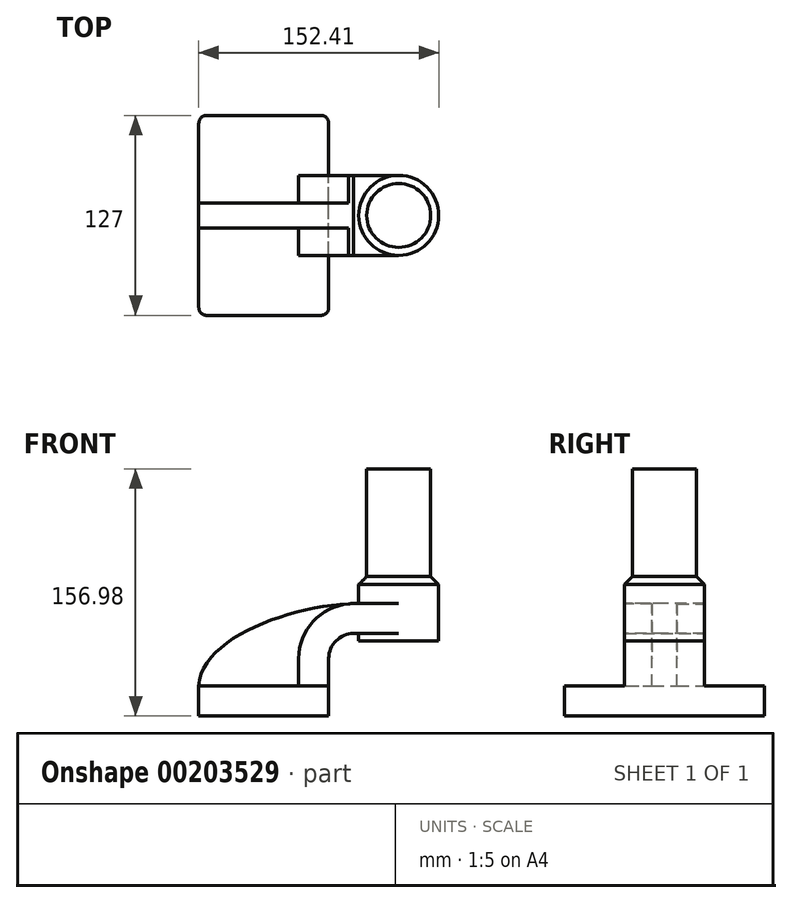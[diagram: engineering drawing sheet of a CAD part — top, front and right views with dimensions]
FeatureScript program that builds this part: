
annotation { "Feature Type Name" : "Feature", "Feature Type Description" : "" }
export const myFeature = defineFeature(function(context is Context, id is Id, definition is map)
    precondition{}
    {
        {
            var Q0;
            Q0=qCreatedBy(makeId("Front.planeOp"),FACE);
            var sketch = newSketch(context, id + "F0", { "sketchPlane" : qUnion([Q0])});
            skLineSegment(sketch, "E0.rect.bottom", {"start": v(-41.28, 9.52) * mm, "end": v(41.28, 9.52) * mm});
            skLineSegment(sketch, "E0.rect.top", {"start": v(-41.28, -9.52) * mm, "end": v(41.28, -9.52) * mm});
            skLineSegment(sketch, "E0.rect.left", {"start": v(-41.28, 9.52) * mm, "end": v(-41.28, -9.52) * mm});
            skLineSegment(sketch, "E0.rect.right", {"start": v(41.28, 9.52) * mm, "end": v(41.28, -9.52) * mm});
            skPoint(sketch, "E0.rect.middle", {"position": v(0, 0) * mm});
            skLineSegment(sketch, "E1", {"start": v(41.28, 9.52) * mm, "end": v(41.28, 27) * mm});
            skArc(sketch, "E2", {"start": v(41.28, 27) * mm, "mid": v(45.92, 38.23) * mm, "end": v(57.15, 42.88) * mm});
            skLineSegment(sketch, "E3", {"start": v(57.15, 42.88) * mm, "end": v(85.72, 42.88) * mm});
            skLineSegment(sketch, "E4.rect.bottom", {"start": v(60.32, 38.1) * mm, "end": v(111.12, 38.1) * mm});
            skLineSegment(sketch, "E4.rect.top", {"start": v(60.32, 66.68) * mm, "end": v(111.12, 66.68) * mm});
            skLineSegment(sketch, "E4.rect.left", {"start": v(60.32, 38.1) * mm, "end": v(60.32, 66.68) * mm});
            skLineSegment(sketch, "E4.rect.right", {"start": v(111.13, 38.1) * mm, "end": v(111.12, 66.68) * mm});
            skPoint(sketch, "E4.rect.middle", {"position": v(85.72, 52.39) * mm});
            skLineSegment(sketch, "E5.0", {"start": v(57.15, 61.93) * mm, "end": v(85.72, 61.93) * mm});
            skArc(sketch, "E5.1", {"start": v(22.23, 27) * mm, "mid": v(32.45, 51.7) * mm, "end": v(57.15, 61.93) * mm});
            skLineSegment(sketch, "E5.2", {"start": v(22.23, 9.52) * mm, "end": v(22.23, 27) * mm});
            skLineSegment(sketch, "E6", {"start": v(85.72, 38.1) * mm, "end": v(85.72, 66.68) * mm});
            skFitSpline(sketch, "E7", {"points": [v(-41.28, 9.53) * mm, v(57.15, 61.93) * mm], "startDerivative": vector(5.2, 92.34) * mm, "endDerivative": vector(120.92, 4.22) * mm});
            skSolve(sketch);
        }
        {
            var Q0;
            Q0=makeQuery(id+"F0.imprint","IMPRINT",FACE,{"disambiguationData":[TD([[makeQuery(id+"F0.imprint","IMPRINT",EDGE,{"derivedFrom":sQuery(id+"F0.wireOp",EDGE,"E0.rect.top")}),1.0]])]});
            extrude(context, id + "F1", {"entities" : qUnion([Q0]), "endBound" : BoundingType.SYMMETRIC, "depth" : 127 * mm});
        }
        {
            var Q0;
            {var subQ9=sQuery(id+"F0.wireOp",EDGE,"E1");Q0=makeQuery(id+"F0.imprint","IMPRINT",FACE,{"disambiguationData":[TD([[makeQuery(id+"F0.imprint","IMPRINT",EDGE,{"derivedFrom":subQ9}),1.0]])]});}
            var Q1;
            {var subQ0=sQuery(id+"F0.wireOp",EDGE,"E6");var subQ1=sQuery(id+"F0.wireOp",EDGE,"E3");var subQ2=makeQuery(id+"F0.imprint","INTERSECT",VERTEX,{"derivedFrom":[subQ1,subQ0]});Q1=makeQuery(id+"F0.imprint","IMPRINT",FACE,{"disambiguationData":[TD([[makeQuery(id+"F0.imprint","IMPRINT",EDGE,{"disambiguationData":[TD([[subQ2,1.0]])],"derivedFrom":subQ1}),1.0]])]});}
            extrude(context, id + "F2", {"entities" : qUnion([Q0, Q1]), "operationType" : NewBodyOperationType.ADD, "endBound" : BoundingType.SYMMETRIC, "depth" : 50.8 * mm});
        }
        {
            var Q0;
            {var subQ3=sQuery(id+"F0.wireOp",EDGE,"E5.2");Q0=makeQuery(id+"F0.imprint","IMPRINT",FACE,{"disambiguationData":[TD([[makeQuery(id+"F0.imprint","IMPRINT",EDGE,{"derivedFrom":subQ3}),1.0]])]});}
            extrude(context, id + "F3", {"entities" : qUnion([Q0]), "operationType" : NewBodyOperationType.ADD, "endBound" : BoundingType.SYMMETRIC, "depth" : 15.88 * mm});
        }
        {
            var Q0;
            {var subQ5=sQuery(id+"F0.wireOp",EDGE,"E4.rect.right");Q0=makeQuery(id+"F0.imprint","IMPRINT",FACE,{"disambiguationData":[TD([[makeQuery(id+"F0.imprint","IMPRINT",EDGE,{"derivedFrom":subQ5}),1.0]])]});}
            var Q1;
            Q1=sQuery(id+"F0.wireOp",EDGE,"E6");
            revolve(context, id + "F4", {"operationType" : NewBodyOperationType.ADD, "entities" : qUnion([Q0]), "axis" : qUnion([Q1]), "revolveType" : RevolveType.FULL});
        }
        {
            var Q0;
            Q0=makeQuery(id+"F1.opExtrude","CAP_EDGE",EDGE,{"disambiguationData":[OSD([sQuery(id+"F0.wireOp",EDGE,"E0.rect.right")])],"isStart":false});
            var Q1;
            Q1=makeQuery(id+"F1.opExtrude","CAP_EDGE",EDGE,{"disambiguationData":[OSD([sQuery(id+"F0.wireOp",EDGE,"E0.rect.left")])],"isStart":false});
            var Q2;
            Q2=makeQuery(id+"F1.opExtrude","CAP_EDGE",EDGE,{"disambiguationData":[OSD([sQuery(id+"F0.wireOp",EDGE,"E0.rect.right")])],"isStart":true});
            var Q3;
            Q3=makeQuery(id+"F1.opExtrude","CAP_EDGE",EDGE,{"disambiguationData":[OSD([sQuery(id+"F0.wireOp",EDGE,"E0.rect.left")])],"isStart":true});
            fillet(context, id + "F5", {"entities" : qUnion([Q0, Q1, Q2, Q3]), "radius" : 5.08 * mm, "tangentPropagation" : true, "allowEdgeOverflow" : false});
        }
        {
            var Q0;
            Q0=makeQuery(id+"F4.opRevolve","SWEPT_FACE",FACE,{"disambiguationData":[OSD([sQuery(id+"F0.wireOp",EDGE,"E4.rect.top")])]});
            extrude(context, id + "F6", {"entities" : qUnion([Q0]), "operationType" : NewBodyOperationType.ADD, "depth" : 12.45 * mm});
        }
        {
            var Q0;
            Q0=makeQuery(id+"F6.opExtrude","CAP_FACE",FACE,{"disambiguationData":[OSD([sQuery(id+"F0.wireOp",EDGE,"E4.rect.top")])],"isStart":false});
            chamfer(context, id + "F7", {"entities" : qUnion([Q0]), "width" : 5.08 * mm, "tangentPropagation" : true});
        }
        {
            var Q0;
            Q0=makeQuery(id+"F6.opExtrude","CAP_FACE",FACE,{"disambiguationData":[OSD([sQuery(id+"F0.wireOp",EDGE,"E4.rect.top")])],"isStart":false});
            extrude(context, id + "F8", {"entities" : qUnion([Q0]), "operationType" : NewBodyOperationType.ADD, "depth" : 25.4 * mm});
        }
        {
            var Q0;
            Q0=makeQuery(id+"F8.opExtrude","CAP_FACE",FACE,{"disambiguationData":[OSD([sQuery(id+"F0.wireOp",EDGE,"E4.rect.top")])],"isStart":false});
            extrude(context, id + "F9", {"entities" : qUnion([Q0]), "operationType" : NewBodyOperationType.ADD, "depth" : 42.93 * mm});
        }
    });
